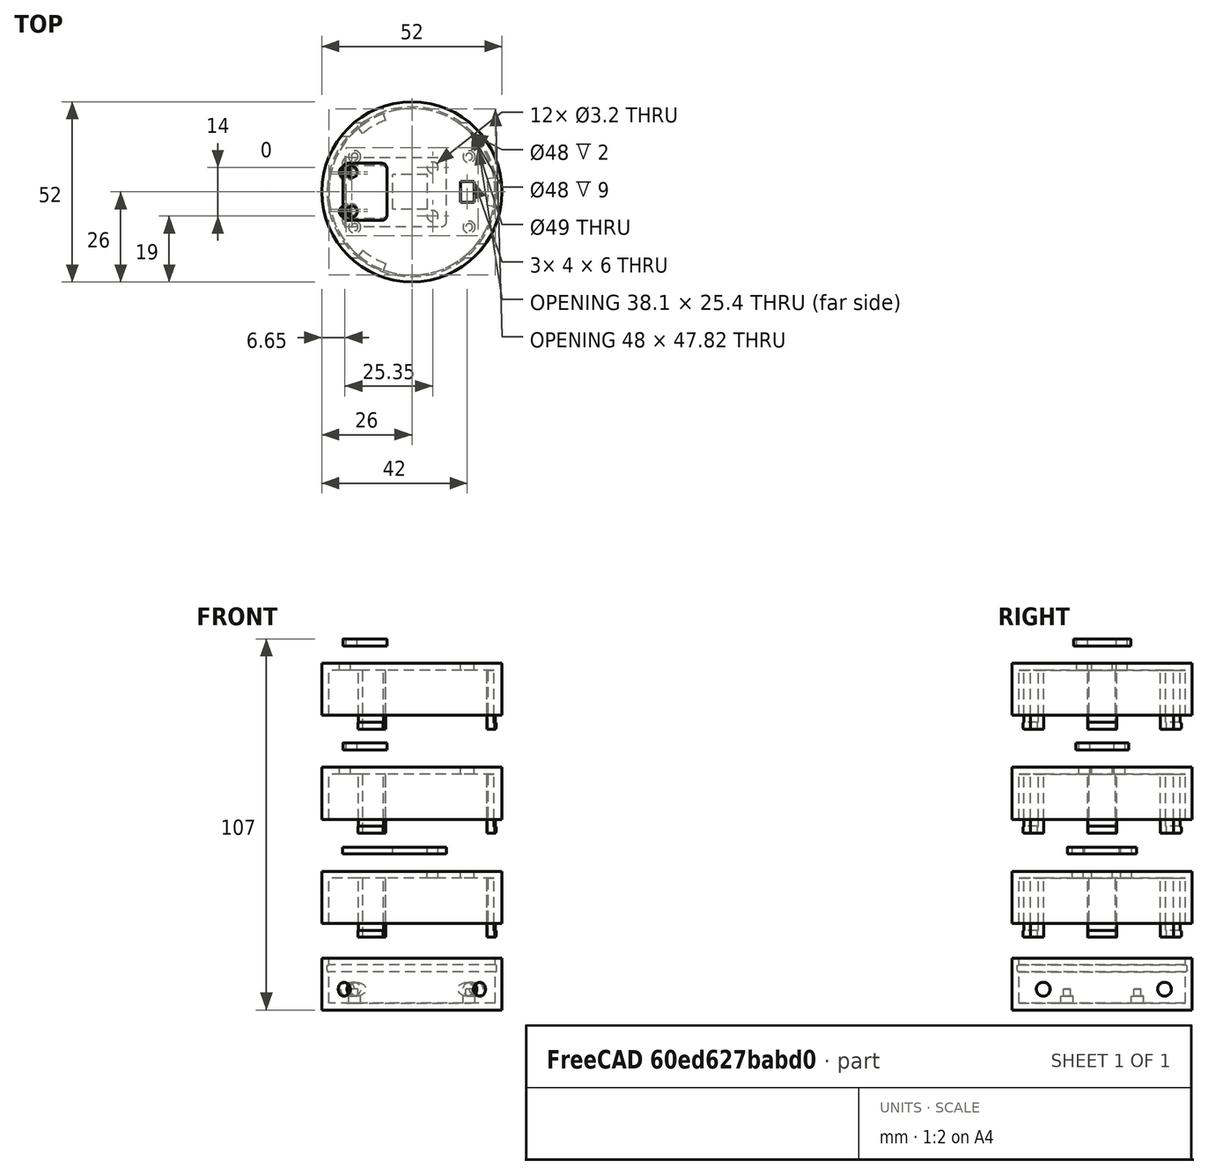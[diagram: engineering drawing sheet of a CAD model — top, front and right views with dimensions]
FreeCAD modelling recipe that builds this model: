
FCSTD DOCUMENT  (FreeCAD 0.19R24291 (Git))
Label: Esp8266_Huzzah_SensorHousing
License: All rights reserved
LicenseURL: http://en.wikipedia.org/wiki/All_rights_reserved
objects: Part::Cylinder×21, Part::Cut×19, Part::Box×10, Part::MultiFuse×10, Part::Fillet×6, Part::Fuse×4, App::DocumentObjectGroup×3
note: 70 computed .brp shape members not serialized (recipe doc carries the construction recipe); baked Part::Feature solids carry a one-line shape summary decoded from their .brp

FEATURE [Part::Box] Box  label="ESP8266MountingBlock"
  AttacherType = Attacher::AttachEngine3D
  Height = 2
  Length = 38.1
  Width = 25.4
FEATURE [Part::Cylinder] Cylinder  label="DistancePieceLowerLeft"
  Angle = 360
  AttacherType = Attacher::AttachEngine3D
  Height = 4
  Placement = pos=(2.54,2.54,0) rot=(0,0,1;0rad)
  Radius = 1.75
FEATURE [Part::Cylinder] Cylinder001  label="MountPieceLowerLeft"
  Angle = 360
  AttacherType = Attacher::AttachEngine3D
  Height = 6
  Placement = pos=(2.54,2.54,0) rot=(0,0,1;0rad)
  Radius = 1
FEATURE [Part::Fuse] Fusion  label="LowerLeftMount"
  Base = -> Cylinder
  Tool = -> Cylinder001
FEATURE [Part::Fuse] Fusion001  label="LowerRightMount"
  Base = -> Cylinder
  Placement = pos=(33.02,0,0) rot=(0,0,1;0rad)
  Tool = -> Cylinder001
FEATURE [Part::Fuse] Fusion002  label="UpperLeftMount"
  Base = -> Cylinder
  Placement = pos=(0,20.32,0) rot=(0,0,1;0rad)
  Tool = -> Cylinder001
FEATURE [Part::Fuse] Fusion003  label="UpperRightMount"
  Base = -> Cylinder
  Placement = pos=(33.02,20.32,0) rot=(0,0,1;0rad)
  Tool = -> Cylinder001
FEATURE [Part::Fillet] Fillet
  Base = -> Box
  Edges = 4 edges r=2: [Edge1,Edge3,Edge5,Edge7]
FEATURE [Part::MultiFuse] Fusion004  label="ESP8266_bracket"
  Placement = pos=(-19.05,-12.7,0) rot=(0,0,1;0rad)
  Shapes = -> [Fusion002,Fusion003,Fillet,Fusion001,Fusion]
FEATURE [Part::Cylinder] Cylinder002  label="LowerHousingOuter"
  Angle = 360
  AttacherType = Attacher::AttachEngine3D
  Height = 15
  Radius = 26
FEATURE [Part::Cylinder] Cylinder003  label="LowerHousingInner"
  Angle = 360
  AttacherType = Attacher::AttachEngine3D
  Height = 15
  Placement = pos=(0,0,2) rot=(0,0,1;0rad)
  Radius = 24
FEATURE [Part::Cut] Cut  label="LowerHousing"
  Base = -> Cylinder002
  Tool = -> Cylinder003
FEATURE [Part::Cylinder] Cylinder004  label="UpperHousingOuter"
  Angle = 360
  AttacherType = Attacher::AttachEngine3D
  Height = 15
  Placement = pos=(0,0,15) rot=(0,0,1;0rad)
  Radius = 26
FEATURE [Part::Cylinder] Cylinder005  label="UpperHousingInner"
  Angle = 360
  AttacherType = Attacher::AttachEngine3D
  Height = 13
  Placement = pos=(0,0,15) rot=(0,0,1;0rad)
  Radius = 24
FEATURE [Part::Cylinder] Cylinder006  label="LowerHousingNotch"
  Angle = 360
  AttacherType = Attacher::AttachEngine3D
  Height = 2
  Placement = pos=(0,0,11) rot=(0,0,1;0rad)
  Radius = 24.5
FEATURE [Part::Cut] Cut002  label="UpperHousing"
  Base = -> Cylinder004
  Tool = -> Cylinder005
FEATURE [Part::Cylinder] Cylinder007  label="UpperHousingCatchOuter"
  Angle = 360
  AttacherType = Attacher::AttachEngine3D
  Height = 17
  Placement = pos=(0,0,11) rot=(0,0,1;0rad)
  Radius = 24
FEATURE [Part::Cylinder] Cylinder008  label="UpperHousingCatch"
  Angle = 360
  AttacherType = Attacher::AttachEngine3D
  Height = 2
  Placement = pos=(0,0,11) rot=(0,0,1;0rad)
  Radius = 24.3
FEATURE [Part::Cylinder] Cylinder009  label="UpperHousingCatchInner"
  Angle = 360
  AttacherType = Attacher::AttachEngine3D
  Height = 17
  Placement = pos=(0,0,11) rot=(0,0,1;0rad)
  Radius = 22
FEATURE [Part::Fillet] Fillet001  label="LowerHousingNotchFillet"
  Base = -> Cylinder006
  Edges = 2 edges r=0.5: [Edge1,Edge3]
FEATURE [Part::Cut] Cut004  label="LowerHousingWithNotch"
  Base = -> Cut
  Tool = -> Fillet001
FEATURE [Part::Fillet] Fillet002
  Base = -> Cylinder008
  Edges = 2 edges r=0.4: [Edge1,Edge3]
FEATURE [Part::MultiFuse] Fusion005
  Shapes = -> [Fillet002,Cylinder007]
FEATURE [Part::Cut] Cut005  label="UpperHousingCompleteCatchCut"
  Base = -> Fusion005
  Tool = -> Cylinder009
FEATURE [Part::Box] Box003  label="DHT22PCB"
  AttacherType = Attacher::AttachEngine3D
  Height = 2
  Length = 30
  Placement = pos=(-20,-10,0) rot=(0,0,1;0rad)
  Width = 20
FEATURE [Part::Cylinder] Cylinder010  label="DHT22PCBMountingLeft"
  Angle = 360
  AttacherType = Attacher::AttachEngine3D
  Height = 10
  Placement = pos=(6,-7,-8) rot=(0,0,1;0rad)
  Radius = 1.6
FEATURE [Part::Cylinder] Cylinder011  label="DHT22PCBMountingRight"
  Angle = 360
  AttacherType = Attacher::AttachEngine3D
  Height = 10
  Placement = pos=(6,7,-8) rot=(0,0,1;0rad)
  Radius = 1.6
FEATURE [Part::Box] Box004  label="DHT22CableHole"
  AttacherType = Attacher::AttachEngine3D
  Height = 10
  Length = 4
  Placement = pos=(14,-3,-8) rot=(0,0,1;0rad)
  Width = 6
FEATURE [Part::Cylinder] Cylinder012  label="UpperHousingCatchCut1"
  Angle = 100
  AttacherType = Attacher::AttachEngine3D
  Height = 28
  Placement = pos=(0,0,0) rot=(0,0,1;0.174533rad)
  Radius = 26
FEATURE [Part::Cylinder] Cylinder013  label="UpperHousingCatchCut2"
  Angle = 100
  AttacherType = Attacher::AttachEngine3D
  Height = 28
  Placement = pos=(0,0,0) rot=(0,0,1;2.26893rad)
  Radius = 26
FEATURE [Part::Cylinder] Cylinder014  label="UpperHousingCatchCut3"
  Angle = 100
  AttacherType = Attacher::AttachEngine3D
  Height = 28
  Placement = pos=(0,0,0) rot=(0,0,-1;1.91986rad)
  Radius = 26
FEATURE [Part::Cut] Cut006  label="UpperHousingSmallCatchCut1"
  Base = -> Cut005
  Tool = -> Cylinder012
FEATURE [Part::Cut] Cut007  label="UpperHousingSmallCatchCut2"
  Base = -> Cut006
  Tool = -> Cylinder013
FEATURE [Part::Cut] Cut008  label="UpperHousingSmallCatch"
  Base = -> Cut007
  Tool = -> Cylinder014
FEATURE [Part::MultiFuse] Fusion008  label="UpperHousingWithCatch"
  Shapes = -> [Cut002,Cut008]
FEATURE [Part::Cylinder] Cylinder015  label="LeftHole"
  Angle = 360
  AttacherType = Attacher::AttachEngine3D
  Height = 60
  Placement = pos=(-30,-17,6) rot=(0,1,0;1.5708rad)
  Radius = 2
FEATURE [Part::Cylinder] Cylinder016  label="RightHole"
  Angle = 360
  AttacherType = Attacher::AttachEngine3D
  Height = 60
  Placement = pos=(-30,18,6) rot=(0,1,0;1.5708rad)
  Radius = 2
FEATURE [Part::Cut] Cut010  label="LowerHousingWithNotchRightHoleCut"
  Base = -> Cut004
  Tool = -> Cylinder016
FEATURE [Part::Cut] Cut011  label="LowerHousingWithNotchAndHoles"
  Base = -> Cut010
  Tool = -> Cylinder015
FEATURE [Part::MultiFuse] Fusion009  label="LowerHousingWithBracket"
  Shapes = -> [Cut011,Fusion004]
FEATURE [Part::MultiFuse] Fusion011  label="DHT22"
  Shapes = -> [Box003,Cylinder010,Cylinder011]
FEATURE [Part::MultiFuse] Fusion012  label="DHT22WithCableHole"
  Placement = pos=(0,0,30) rot=(0,0,1;0rad)
  Shapes = -> [Fusion011,Box004]
FEATURE [Part::Cut] Cut012  label="UpperHousingDHT22"
  Base = -> Fusion008
  Placement = pos=(0,0,10) rot=(0,0,1;0rad)
  Tool = -> Fusion012
FEATURE [Part::Cut] Cut013  label="DHT22LeftMountCut"
  Base = -> Box003
  Tool = -> Cylinder010
FEATURE [Part::Cut] Cut014  label="DHT22RightMountCut"
  Base = -> Cut013
  Tool = -> Cylinder011
FEATURE [Part::Fillet] Fillet003
  Base = -> Cut014
  Edges = 4 edges r=1.5: [Edge1,Edge3,Edge6,Edge13]
FEATURE [Part::Box] Box005  label="DHT22PinCut"
  AttacherType = Attacher::AttachEngine3D
  Height = 10
  Length = 10
  Placement = pos=(-5.5,-5,0) rot=(0,0,1;0rad)
  Width = 10
FEATURE [Part::Cut] Cut015  label="DHT22Spacer"
  Base = -> Fillet003
  Placement = pos=(0,0,45) rot=(0,0,1;0rad)
  Tool = -> Box005
FEATURE [Part::Box] Box006  label="Si7021PCB"
  AttacherType = Attacher::AttachEngine3D
  Height = 2
  Length = 17.78
  Placement = pos=(-8.89,-7.62,0) rot=(0,0,1;0rad)
  Width = 15.24
FEATURE [Part::Cylinder] Cylinder017  label="Si7021PCBMountingLeft"
  Angle = 360
  AttacherType = Attacher::AttachEngine3D
  Height = 10
  Placement = pos=(-17.35,5.08,-8) rot=(0,0,1;0rad)
  Radius = 1.6
FEATURE [Part::Cylinder] Cylinder018  label="Si7021PCBMountingRight"
  Angle = 360
  AttacherType = Attacher::AttachEngine3D
  Height = 10
  Placement = pos=(-17.35,-5.08,-8) rot=(0,0,1;0rad)
  Radius = 1.6
FEATURE [Part::Box] Box007  label="Si7021CableHole"
  AttacherType = Attacher::AttachEngine3D
  Height = 10
  Length = 4
  Placement = pos=(14,-3,-8) rot=(0,0,1;0rad)
  Width = 6
FEATURE [Part::MultiFuse] Fusion013  label="Si7021"
  Placement = pos=(-2,0,0) rot=(0,0,1;0rad)
  Shapes = -> [Box006,Cylinder018,Cylinder017]
FEATURE [Part::MultiFuse] Fusion014  label="Si7021WithCableHole"
  Placement = pos=(0,0,30) rot=(0,0,1;0rad)
  Shapes = -> [Fusion013,Box007]
FEATURE [Part::Cut] Cut016  label="UpperHousingSi7021"
  Base = -> Fusion008
  Placement = pos=(0,0,40) rot=(0,0,1;0rad)
  Tool = -> Fusion014
FEATURE [Part::Box] Box008  label="Si7021PCBShort"
  AttacherType = Attacher::AttachEngine3D
  Height = 2
  Length = 12.7
  Placement = pos=(-19.89,-7.62,0) rot=(0,0,1;0rad)
  Width = 15.24
FEATURE [Part::Cut] Cut017  label="Si7021PCBMountingRight001"
  Base = -> Box008
  Tool = -> Cylinder018
FEATURE [Part::Cut] Cut018  label="Si7021PCBMountingLeft001"
  Base = -> Cut017
  Tool = -> Cylinder017
FEATURE [Part::Fillet] Fillet004  label="Si7021Spacer"
  Base = -> Cut018
  Edges = 4 edges r=1.5: [Edge1,Edge3,Edge6,Edge13]
  Placement = pos=(0,0,75) rot=(0,0,1;0rad)
FEATURE [App::DocumentObjectGroup] Gruppe  label="DHT023"
  Group = -> [Cut015,Cut012]
FEATURE [App::DocumentObjectGroup] Gruppe001  label="Si7023"
  Group = -> [Cut016,Fillet004]
FEATURE [Part::Box] Box009  label="HTU21DPCB"
  AttacherType = Attacher::AttachEngine3D
  Height = 2
  Length = 17.78
  Placement = pos=(-8.89,-8.255,0) rot=(0,0,1;0rad)
  Width = 16.51
FEATURE [Part::Cylinder] Cylinder019  label="HTU21DPCBMountingLeft"
  Angle = 360
  AttacherType = Attacher::AttachEngine3D
  Height = 10
  Placement = pos=(-17.35,5.715,-8) rot=(0,0,1;0rad)
  Radius = 1.6
FEATURE [Part::Cylinder] Cylinder020  label="HTU21DPCBMountingRight"
  Angle = 360
  AttacherType = Attacher::AttachEngine3D
  Height = 10
  Placement = pos=(-17.35,-5.71,-8) rot=(0,0,1;0rad)
  Radius = 1.6
FEATURE [Part::Box] Box010  label="HTU21DCableHole"
  AttacherType = Attacher::AttachEngine3D
  Height = 10
  Length = 4
  Placement = pos=(14,-3,-8) rot=(0,0,1;0rad)
  Width = 6
FEATURE [Part::MultiFuse] Fusion016  label="HTU21D"
  Placement = pos=(-2,0,0) rot=(0,0,1;0rad)
  Shapes = -> [Box009,Cylinder020,Cylinder019]
FEATURE [Part::MultiFuse] Fusion015  label="HTU21DWithCableHole"
  Placement = pos=(0,0,30) rot=(0,0,1;0rad)
  Shapes = -> [Fusion016,Box010]
FEATURE [Part::Cut] Cut019  label="UpperHousingHTU21D-F"
  Base = -> Fusion008
  Placement = pos=(0,0,70) rot=(0,0,1;0rad)
  Tool = -> Fusion015
FEATURE [Part::Box] Box011  label="HTU21DPCBShort"
  AttacherType = Attacher::AttachEngine3D
  Height = 2
  Length = 12.7
  Placement = pos=(-19.89,-8.26,0) rot=(0,0,1;0rad)
  Width = 16.51
FEATURE [Part::Cut] Cut020  label="HTU21DPCBMountingRight001"
  Base = -> Box011
  Tool = -> Cylinder020
FEATURE [Part::Cut] Cut021  label="HTU21DPCBMountingLeft001"
  Base = -> Cut020
  Tool = -> Cylinder019
FEATURE [Part::Fillet] Fillet005  label="HTU21DSpacer"
  Base = -> Cut021
  Edges = 4 edges r=1.5: [Edge1,Edge3,Edge6,Edge13]
  Placement = pos=(0,0,105) rot=(0,0,1;0rad)
FEATURE [App::DocumentObjectGroup] Gruppe002  label="HTU21D-F"
  Group = -> [Cut019,Fillet005]
